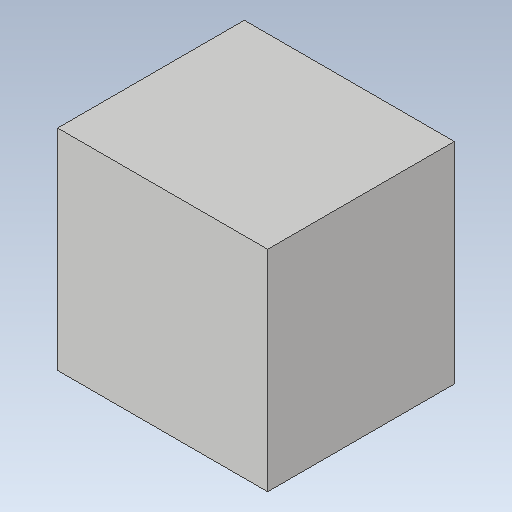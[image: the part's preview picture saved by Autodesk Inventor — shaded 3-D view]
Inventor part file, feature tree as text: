
AUTODESK INVENTOR PART (.ipt)
format: ipt  version: 2020 (Build 240168000, 168)  size: 92,160 bytes
history: native  units: mm
features: extrude x2, sketch x2
ambient origin geometry x8: Origin, YZ Plane, XZ Plane, XY Plane, X Axis, Y Axis, Z Axis, Center Point
bodies: Solid1 (feature_tree)
feature tree (4):
  extrude  "Extrusion1"  Depth=180.0mm
  extrude  "Extrusion2"  Depth=180.0mm TaperAngle=0.0deg
  sketch  "Sketch1"  dims[d0=180.0mm d1=180.0mm]
  sketch  "Sketch2"  dims[d2=180.0mm d3=0.0mm d4=20.0mm d5=0.0mm]
